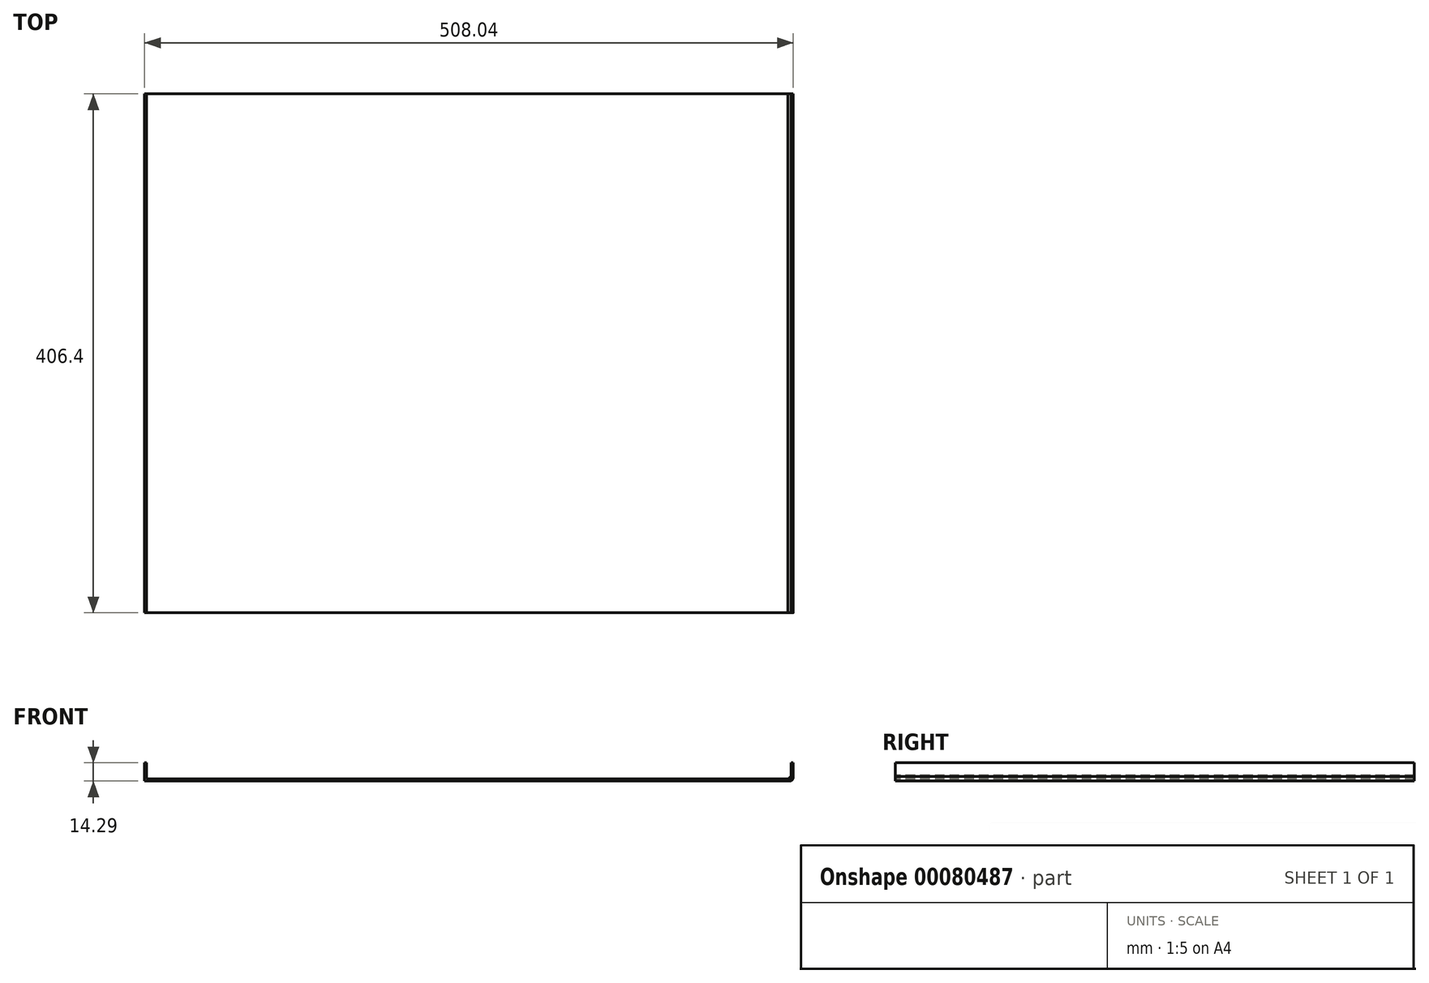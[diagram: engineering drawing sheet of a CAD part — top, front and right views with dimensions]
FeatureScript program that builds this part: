
annotation { "Feature Type Name" : "Feature", "Feature Type Description" : "" }
export const myFeature = defineFeature(function(context is Context, id is Id, definition is map)
    precondition{}
    {
        {
            var Q0;
            Q0=qCreatedBy(makeId("Front.planeOp"),FACE);
            var sketch = newSketch(context, id + "F0", { "sketchPlane" : qUnion([Q0])});
            skLineSegment(sketch, "E0.bottom", {"start": v(0, 0) * mm, "end": v(508, 0) * mm});
            skLineSegment(sketch, "E0.right", {"start": v(508, 0) * mm, "end": v(508, 1.59) * mm});
            skLineSegment(sketch, "E1.left", {"start": v(-4.11, 4.02) * mm, "end": v(-4.11, 4.06) * mm});
            skLineSegment(sketch, "E1.right", {"start": v(0, 4.02) * mm, "end": v(0, 4.06) * mm});
            skLineSegment(sketch, "E2.0", {"start": v(0, 1.59) * mm, "end": v(508, 1.59) * mm});
            skLineSegment(sketch, "E3", {"start": v(0, 1.59) * mm, "end": v(0, 0) * mm});
            skSolve(sketch);
        }
        {
            var Q0;
            Q0 = qSketchRegion(id + "F0", true);
            extrude(context, id + "F1", {"entities" : qUnion([Q0]), "depth" : 406.4 * mm});
        }
        {
            var Q0;
            Q0=makeQuery(id+"F1.opExtrude","CAP_FACE",FACE,{"disambiguationData":[OSD([sQuery(id+"F0.wireOp",EDGE,"E0.bottom"),sQuery(id+"F0.wireOp",EDGE,"E0.right"),sQuery(id+"F0.wireOp",EDGE,"E2.0"),sQuery(id+"F0.wireOp",EDGE,"E3")])],"isStart":false});
            var sketch = newSketch(context, id + "F2", { "sketchPlane" : qUnion([Q0])});
            skLineSegment(sketch, "E4.bottom", {"start": v(0, 1.59) * mm, "end": v(0, 1.59) * mm});
            skLineSegment(sketch, "E4.top", {"start": v(0, 14.29) * mm, "end": v(0, 14.29) * mm});
            skLineSegment(sketch, "E4.left", {"start": v(0, 1.59) * mm, "end": v(0, 14.29) * mm});
            skLineSegment(sketch, "E4.right", {"start": v(0, 1.59) * mm, "end": v(0, 14.29) * mm});
            skLineSegment(sketch, "E5.bottom", {"start": v(0, 14.29) * mm, "end": v(1.6, 14.29) * mm});
            skLineSegment(sketch, "E5.top", {"start": v(0, 1.59) * mm, "end": v(1.6, 1.59) * mm});
            skLineSegment(sketch, "E5.left", {"start": v(0, 14.29) * mm, "end": v(0, 1.59) * mm});
            skLineSegment(sketch, "E5.right", {"start": v(1.6, 14.29) * mm, "end": v(1.6, 1.59) * mm});
            skLineSegment(sketch, "E6.right", {"start": v(0, 9.37) * mm, "end": v(0, 9.9) * mm});
            skLineSegment(sketch, "E7.bottom", {"start": v(508, 1.59) * mm, "end": v(506.41, 1.59) * mm});
            skLineSegment(sketch, "E7.top", {"start": v(508, 14.29) * mm, "end": v(506.41, 14.29) * mm});
            skLineSegment(sketch, "E7.left", {"start": v(508, 1.59) * mm, "end": v(508, 14.29) * mm});
            skLineSegment(sketch, "E7.right", {"start": v(506.41, 1.59) * mm, "end": v(506.41, 14.29) * mm});
            skArc(sketch, "E8", {"start": v(503.87, 1.59) * mm, "mid": v(505.36, 2.83) * mm, "end": v(506.41, 4.47) * mm});
            skArc(sketch, "E9", {"start": v(505.8, 0) * mm, "mid": v(507.57, 1.43) * mm, "end": v(508, 3.67) * mm});
            skSolve(sketch);
        }
        {
            var Q0;
            {var subQ3=sQuery(id+"F2.wireOp",EDGE,"E5.bottom");Q0=makeQuery(id+"F2.imprint","IMPRINT",FACE,{"disambiguationData":[TD([[makeQuery(id+"F2.imprint","IMPRINT",EDGE,{"derivedFrom":subQ3}),-1.0]])]});}
            extrude(context, id + "F3", {"entities" : qUnion([Q0]), "oppositeDirection" : true, "depth" : 406.4 * mm});
        }
        {
            var Q0;
            Q0 = qSketchRegion(id + "F2", true);
            extrude(context, id + "F4", {"entities" : qUnion([Q0]), "operationType" : NewBodyOperationType.ADD, "oppositeDirection" : true, "depth" : 406.4 * mm});
        }
        {
            var Q0;
            {var subQ3=sQuery(id+"F2.wireOp",EDGE,"E8");Q0=makeQuery(id+"F2.imprint","IMPRINT",FACE,{"disambiguationData":[TD([[makeQuery(id+"F2.imprint","IMPRINT",EDGE,{"derivedFrom":subQ3}),-1.0]])]});}
            extrude(context, id + "F5", {"entities" : qUnion([Q0]), "oppositeDirection" : true, "depth" : 406.4 * mm});
        }
        {
            var Q0;
            {var subQ1=makeQuery(id+"F1.opExtrude","CAP_EDGE",EDGE,{"disambiguationData":[OSD([sQuery(id+"F0.wireOp",EDGE,"E0.right")])],"isStart":false});Q0=makeQuery(id+"F2.imprint","IMPRINT",FACE,{"disambiguationData":[TD([[makeQuery(id+"F2.imprint","IMPRINT",EDGE,{"derivedFrom":subQ1}),1.0]])]});}
            var Q1;
            {var subQ0=sQuery(id+"F2.wireOp",EDGE,"E7.left");var subQ3=sQuery(id+"F2.wireOp",EDGE,"E9");var subQ5=makeQuery(id+"F2.imprint","INTERSECT",VERTEX,{"disambiguationData":[OD(1.0)],"derivedFrom":[subQ0,subQ3]});Q1=makeQuery(id+"F2.imprint","IMPRINT",FACE,{"disambiguationData":[TD([[makeQuery(id+"F2.imprint","IMPRINT",EDGE,{"disambiguationData":[TD([[subQ5,1.0]])],"derivedFrom":subQ3}),-1.0]])]});}
            extrude(context, id + "F6", {"entities" : qUnion([Q0, Q1]), "operationType" : NewBodyOperationType.REMOVE, "endBound" : BoundingType.THROUGH_ALL, "oppositeDirection" : true, "depth" : 25.4 * mm});
        }
    });
